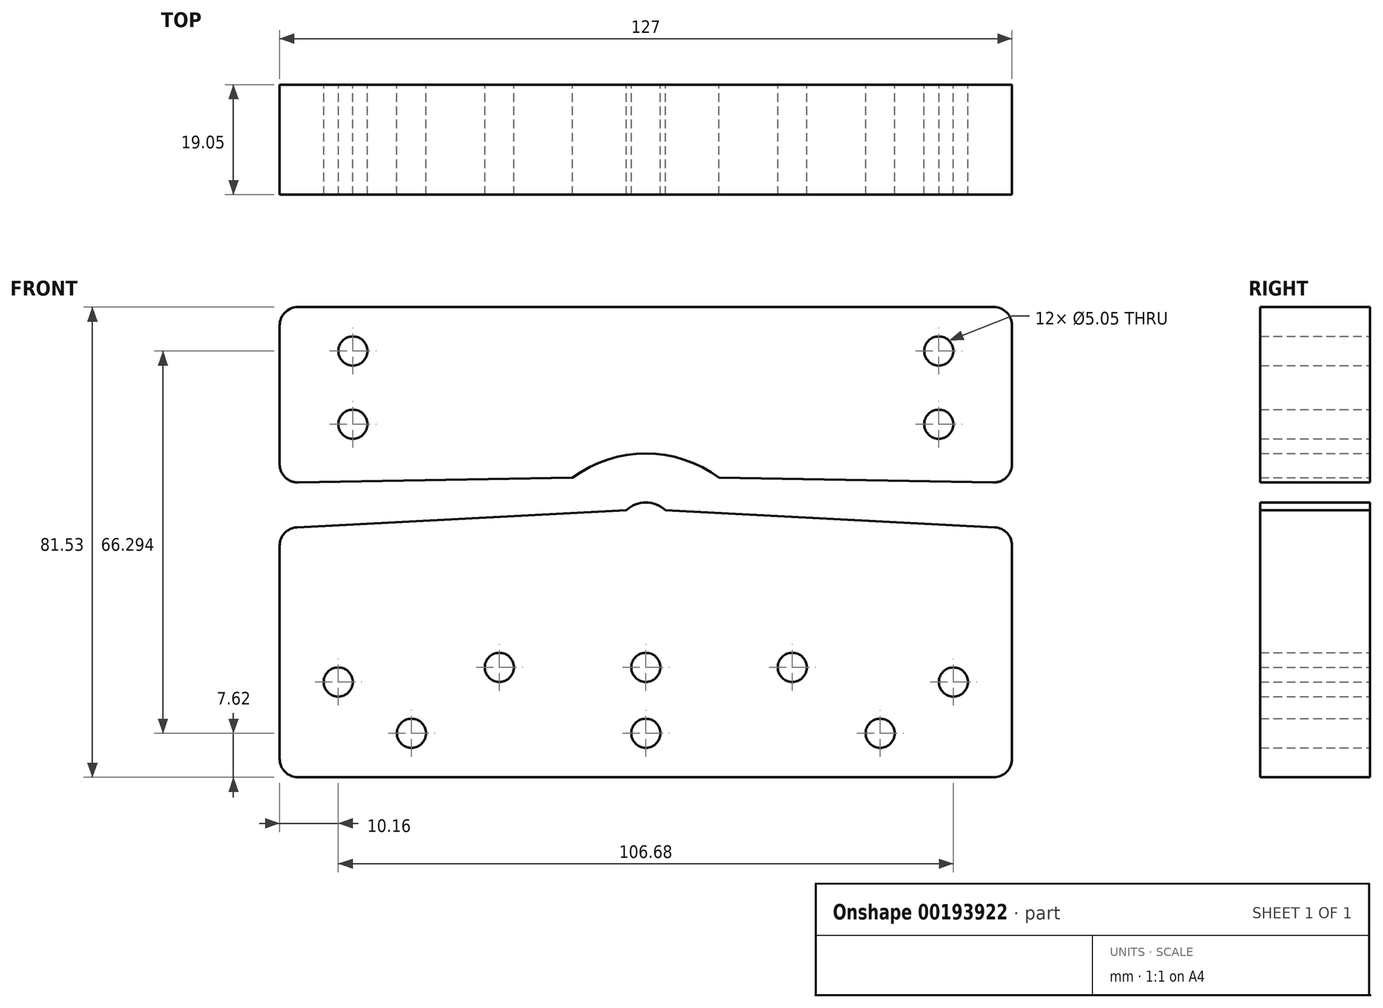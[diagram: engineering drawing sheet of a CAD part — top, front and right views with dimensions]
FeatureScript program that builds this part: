
annotation { "Feature Type Name" : "Feature", "Feature Type Description" : "" }
export const myFeature = defineFeature(function(context is Context, id is Id, definition is map)
    precondition{}
    {
        {
            var Q0;
            Q0=qCreatedBy(makeId("Front.planeOp"),FACE);
            var sketch = newSketch(context, id + "F0", { "sketchPlane" : qUnion([Q0])});
            skLineSegment(sketch, "E0.top", {"start": v(-60.33, 0) * mm, "end": v(60.33, 0) * mm});
            skLineSegment(sketch, "E0.left", {"start": v(-63.5, 40.17) * mm, "end": v(-63.5, 3.17) * mm});
            skLineSegment(sketch, "E0.right", {"start": v(63.5, 40.17) * mm, "end": v(63.5, 3.18) * mm});
            skLineSegment(sketch, "E1.top", {"start": v(-60.33, 81.53) * mm, "end": v(60.33, 81.53) * mm});
            skLineSegment(sketch, "E1.left", {"start": v(-63.5, 54.28) * mm, "end": v(-63.5, 78.36) * mm});
            skLineSegment(sketch, "E1.right", {"start": v(63.5, 54.28) * mm, "end": v(63.5, 78.36) * mm});
            skCircle(sketch, "E2", {"center": v(0, 19.05) * mm, "radius": 2.53 * mm});
            skCircle(sketch, "E3", {"center": v(-53.34, 16.5) * mm, "radius": 2.53 * mm});
            skCircle(sketch, "E4", {"center": v(-25.4, 19.05) * mm, "radius": 2.53 * mm});
            skCircle(sketch, "E5", {"center": v(25.4, 19.05) * mm, "radius": 2.53 * mm});
            skCircle(sketch, "E6", {"center": v(53.34, 16.5) * mm, "radius": 2.53 * mm});
            skCircle(sketch, "E7", {"center": v(-40.64, 7.62) * mm, "radius": 2.53 * mm});
            skCircle(sketch, "E8", {"center": v(40.64, 7.62) * mm, "radius": 2.53 * mm});
            skCircle(sketch, "E9", {"center": v(0, 7.62) * mm, "radius": 2.53 * mm});
            skCircle(sketch, "E10", {"center": v(-50.8, 73.91) * mm, "radius": 2.53 * mm});
            skCircle(sketch, "E11", {"center": v(50.8, 73.91) * mm, "radius": 2.53 * mm});
            skCircle(sketch, "E12", {"center": v(-50.8, 61.21) * mm, "radius": 2.53 * mm});
            skCircle(sketch, "E13", {"center": v(50.8, 61.21) * mm, "radius": 2.53 * mm});
            skPoint(sketch, "E14.visualSharp", {"position": v(-63.5, 81.53) * mm});
            skArc(sketch, "E14.filletArc", {"start": v(-60.33, 81.53) * mm, "mid": v(-62.57, 80.6) * mm, "end": v(-63.5, 78.36) * mm});
            skPoint(sketch, "E15.visualSharp", {"position": v(63.5, 81.53) * mm});
            skArc(sketch, "E15.filletArc", {"start": v(63.5, 78.36) * mm, "mid": v(62.57, 80.6) * mm, "end": v(60.33, 81.53) * mm});
            skPoint(sketch, "E16.visualSharp", {"position": v(63.5, 0) * mm});
            skArc(sketch, "E16.filletArc", {"start": v(60.33, 0) * mm, "mid": v(62.57, 0.93) * mm, "end": v(63.5, 3.18) * mm});
            skPoint(sketch, "E17.visualSharp", {"position": v(-63.5, 0) * mm});
            skArc(sketch, "E17.filletArc", {"start": v(-63.5, 3.17) * mm, "mid": v(-62.57, 0.93) * mm, "end": v(-60.33, 0) * mm});
            skLineSegment(sketch, "E18", {"start": v(-60.27, 51.11) * mm, "end": v(-12.7, 51.94) * mm});
            skLineSegment(sketch, "E19", {"start": v(12.7, 51.94) * mm, "end": v(60.27, 51.11) * mm});
            skArc(sketch, "E20", {"start": v(3.39, 46.33) * mm, "mid": v(0, 47.62) * mm, "end": v(-3.39, 46.33) * mm});
            skLineSegment(sketch, "E21", {"start": v(-60.5, 43.34) * mm, "end": v(-3.39, 46.33) * mm});
            skLineSegment(sketch, "E22", {"start": v(60.5, 43.34) * mm, "end": v(3.39, 46.33) * mm});
            skArc(sketch, "E23", {"start": v(12.7, 51.94) * mm, "mid": v(0, 56.13) * mm, "end": v(-12.7, 51.94) * mm});
            skPoint(sketch, "E24.visualSharp", {"position": v(-63.5, 43.18) * mm});
            skArc(sketch, "E24.filletArc", {"start": v(-60.5, 43.34) * mm, "mid": v(-62.63, 42.35) * mm, "end": v(-63.5, 40.17) * mm});
            skPoint(sketch, "E25.visualSharp", {"position": v(-63.5, 51.05) * mm});
            skArc(sketch, "E25.filletArc", {"start": v(-63.5, 54.28) * mm, "mid": v(-62.55, 52.02) * mm, "end": v(-60.27, 51.11) * mm});
            skPoint(sketch, "E26.visualSharp", {"position": v(63.5, 51.05) * mm});
            skArc(sketch, "E26.filletArc", {"start": v(60.27, 51.11) * mm, "mid": v(62.55, 52.02) * mm, "end": v(63.5, 54.28) * mm});
            skPoint(sketch, "E27.visualSharp", {"position": v(63.5, 43.18) * mm});
            skArc(sketch, "E27.filletArc", {"start": v(63.5, 40.17) * mm, "mid": v(62.63, 42.35) * mm, "end": v(60.5, 43.34) * mm});
            skSolve(sketch);
        }
        {
            var Q0;
            {var subQ0=sQuery(id+"F0.wireOp",EDGE,"E0.top");Q0=makeQuery(id+"F0.imprint","IMPRINT",FACE,{"disambiguationData":[TD([[makeQuery(id+"F0.imprint","IMPRINT",EDGE,{"derivedFrom":subQ0}),1.0]])]});}
            var Q1;
            Q1=makeQuery(id+"F0.imprint","IMPRINT",FACE,{"disambiguationData":[TD([[makeQuery(id+"F0.imprint","IMPRINT",EDGE,{"derivedFrom":sQuery(id+"F0.wireOp",EDGE,"E1.top")}),-1.0]])]});
            extrude(context, id + "F1", {"entities" : qUnion([Q0, Q1]), "depth" : 19.05 * mm});
        }
    });
